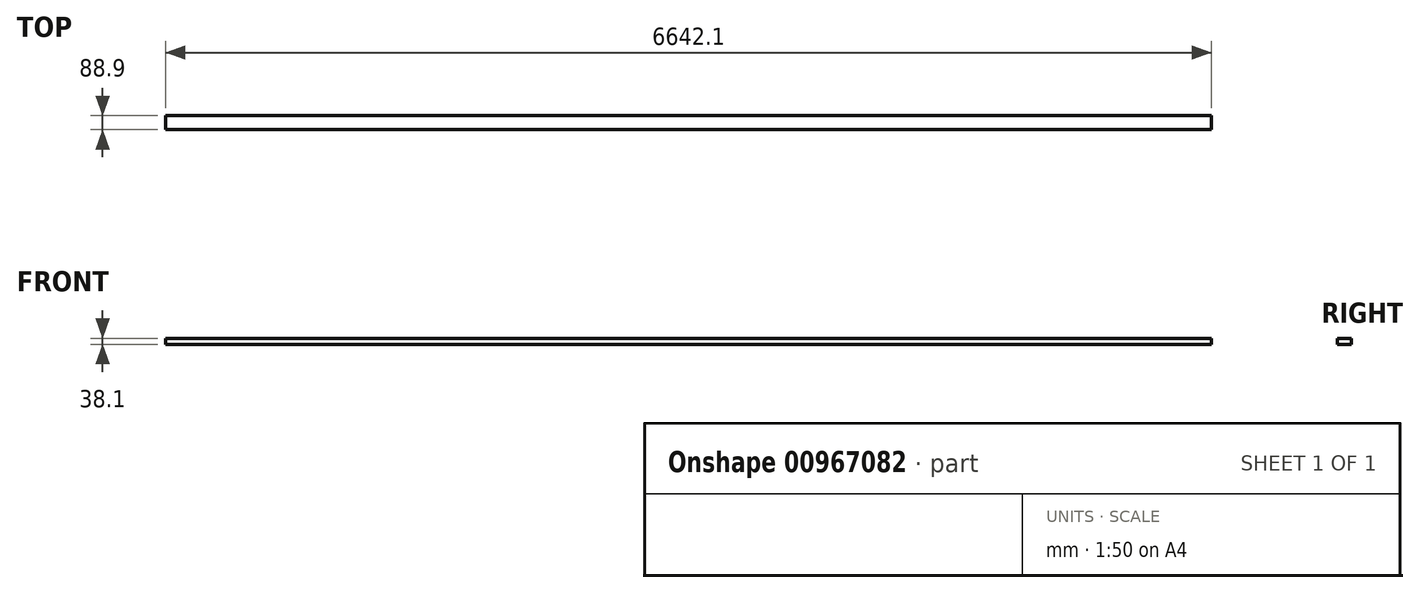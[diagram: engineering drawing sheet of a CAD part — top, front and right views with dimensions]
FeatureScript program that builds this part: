
annotation { "Feature Type Name" : "Feature", "Feature Type Description" : "" }
export const myFeature = defineFeature(function(context is Context, id is Id, definition is map)
    precondition{}
    {
        {
            var Q0;
            Q0=qCreatedBy(makeId("Right.planeOp"),FACE);
            var sketch = newSketch(context, id + "F0", { "sketchPlane" : qUnion([Q0])});
            skLineSegment(sketch, "E0.bottom", {"start": v(0, 0) * mm, "end": v(88.9, 0) * mm});
            skLineSegment(sketch, "E0.top", {"start": v(0, 38.1) * mm, "end": v(88.9, 38.1) * mm});
            skLineSegment(sketch, "E0.left", {"start": v(0, 0) * mm, "end": v(0, 38.1) * mm});
            skLineSegment(sketch, "E0.right", {"start": v(88.9, 0) * mm, "end": v(88.9, 38.1) * mm});
            skSolve(sketch);
        }
        {
            var Q0;
            Q0=qSketchRegion(id+"F0",true);
            extrude(context, id + "F1", {"entities" : qUnion([Q0]), "oppositeDirection" : true, "depth" : 6642.1 * mm, "offsetDistance" : 25.4 * mm});
        }
    });
